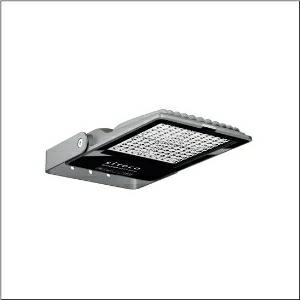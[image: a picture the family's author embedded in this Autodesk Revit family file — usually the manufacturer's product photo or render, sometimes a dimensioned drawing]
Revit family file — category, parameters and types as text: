
# Revit family: sicompact_r__31_mini___pl32_5xa7571c1k23_a489
name_source: partatom
category: Lighting Fixtures
units: mm (PartAtom-declared; Revit-internal decimal feet)

## family parameters
Cut with Voids When Loaded = No
Host = Face
Light Source = No
Part Type = Normal
Room Calculation Point = No
Round Connector Dimension = Use Diameter
Shared = No

## types (1)
- SiCompact® 31 mini  PL32 (1 x LED, 15000 lm, 100 W, 3000K)
    Apparent Load = 100 VA
    CIE Flux Codes = 32 69 98 100 100
    Color Rendering = 70
    Color Temperature = 3000K
    Default Elevation = 1800 mm
    Description = SiCompact® 31 mini, floodlight, primary light control with lens, of plastic, of toughened safety glass, transparent, light distribution: PL32, light emission: direct distribution, primary light characteristic: asymmetric, installation type: surface-mounted, LED, High Power LED, rated luminous flux: 15.000lm, luminous efficacy: 150lm/W, light colour: 730, colour temperature: 3000K, control gear: ON/OFF, with cable, 3x 1.5mm², mains connection: 220..240V, AC, 50/60Hz, connection cable pre-assembled, cable length: 2m, rated input power: 100W, of diecast aluminium, specular, metallic grey (RAL 9006), length: 461mm, width: 261mm, height: 62mm, bracket, of sheet steel, coated, metallic grey (RAL 9006), ON/OFF, protection rating (complete): IP66, insulation class (complete): insulation class I (protective earthing), certification: CE, ENEC, impact resistance: IK08, permissible operating ambient temperature: -40..+45°C, packaging unit: 1 piece

Light Distribution: PL32
    Height = 62 mm  [stored 0.203412 ft]
    Lamp = 1 x LED
    Lamp Light Flux = 15000 lm
    Lamp Power = 100 W
    Lamp count = 1
    Length = 460 mm
    Luminous efficacy = 150 lm/W
    Manufacturer = Siteco
    ModVariant = No
    Model = 5XA7571C1K23
    Mounting Place = Wall
    Mounting Type = Surface mounted
    Number of Poles = 1
    OnlyDefault = Yes
    Power Factor = 1
    Product Name = SiCompact® 31 mini | PL32
    Product group = floodlight | wall mounted
    ProductGroupID = 2001
    Protection Class = Protection class I
    Protection Degree = IP 66
    RLX_Detail_Level = 1
    RLX_Emergency_Light_Flux = 0 lm
    RLX_Emergency_Type = 0
    RLX_Emergency_Type_DB = No
    RlxData = <blob elided: 127045 chars, md5=d8b57d14>
    Socket = socket
    Standby Power = 0 W
    System Light Flux = 15000 lm
    System Power = 100 W
    Type Comments = Product without accessories
    Type Image = l_1006951.jpg
    URL = http://relux.com
    VarID = ---
    Voltage = 0 V
    Weight = 0.00 kg
    Width = 260 mm

note: [stored X ft] marks values corroborated as IEEE doubles in the binary element streams (Revit-internal decimal feet)

## geometry (parser evidence)
native form markers: Blend x4, Sweep x13
no freeform markers — native parametric forms only
